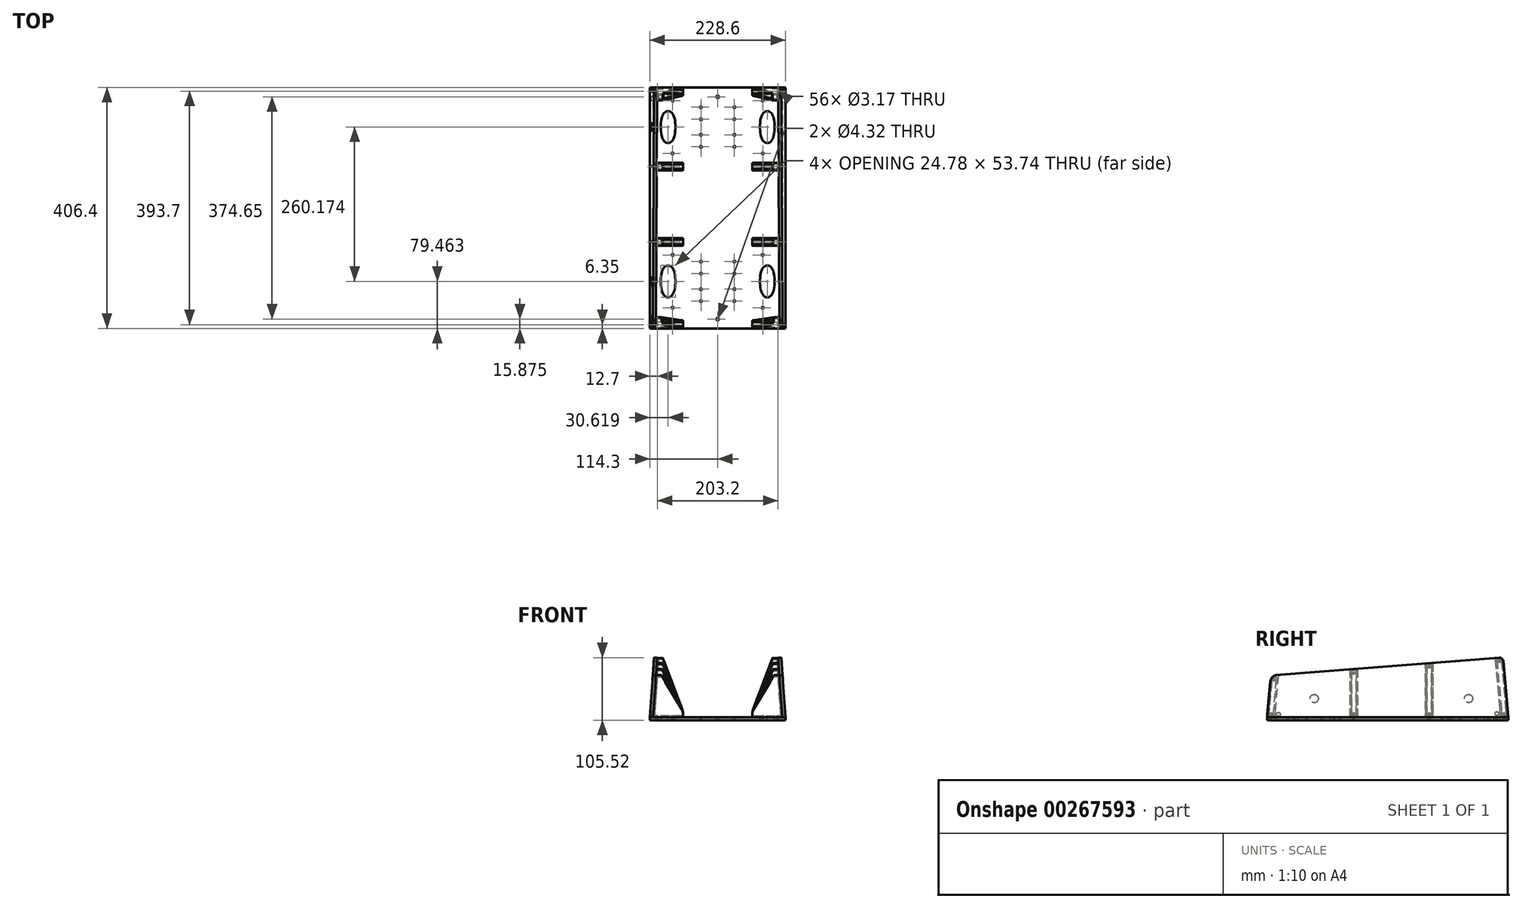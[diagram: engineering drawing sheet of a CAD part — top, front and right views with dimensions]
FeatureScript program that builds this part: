
annotation { "Feature Type Name" : "Feature", "Feature Type Description" : "" }
export const myFeature = defineFeature(function(context is Context, id is Id, definition is map)
    precondition{}
    {
        {
            var Q0;
            Q0=qCreatedBy(makeId("Top.planeOp"),FACE);
            var sketch = newSketch(context, id + "F0", { "sketchPlane" : qUnion([Q0])});
            skLineSegment(sketch, "E0.bottom", {"start": v(-114.3, 203.2) * mm, "end": v(114.3, 203.2) * mm});
            skLineSegment(sketch, "E0.top", {"start": v(-114.3, -203.2) * mm, "end": v(114.3, -203.2) * mm});
            skLineSegment(sketch, "E0.left", {"start": v(-114.3, 203.2) * mm, "end": v(-114.3, -203.2) * mm});
            skLineSegment(sketch, "E0.right", {"start": v(114.3, 203.2) * mm, "end": v(114.3, -203.2) * mm});
            skPoint(sketch, "E0.middle", {"position": v(0, 0) * mm});
            skSolve(sketch);
        }
        {
            var Q0;
            Q0=makeQuery(id+"F0.imprint","IMPRINT",FACE,{"disambiguationData":[TD([[makeQuery(id+"F0.imprint","IMPRINT",EDGE,{"derivedFrom":sQuery(id+"F0.wireOp",EDGE,"E0.bottom")}),-1.0]])]});
            extrude(context, id + "F1", {"entities" : qUnion([Q0]), "depth" : 5.08 * mm});
        }
        {
            var Q0;
            Q0=makeQuery(id+"F1.opExtrude","SWEPT_FACE",FACE,{"disambiguationData":[OSD([sQuery(id+"F0.wireOp",EDGE,"E0.bottom")])]});
            var sketch = newSketch(context, id + "F2", { "sketchPlane" : qUnion([Q0])});
            skLineSegment(sketch, "E1", {"start": v(114.3, 5.08) * mm, "end": v(107.2, 106.68) * mm});
            skLineSegment(sketch, "E2", {"start": v(107.2, 106.68) * mm, "end": v(102.13, 106.33) * mm});
            skLineSegment(sketch, "E3", {"start": v(102.13, 106.33) * mm, "end": v(109.2, 5.08) * mm});
            skLineSegment(sketch, "E4", {"start": v(109.2, 5.08) * mm, "end": v(114.3, 5.08) * mm});
            skSolve(sketch);
        }
        {
            var Q0;
            Q0=makeQuery(id+"F1.opExtrude","SWEPT_FACE",FACE,{"disambiguationData":[OSD([sQuery(id+"F0.wireOp",EDGE,"E0.top")])]});
            var sketch = newSketch(context, id + "F3", { "sketchPlane" : qUnion([Q0])});
            skLineSegment(sketch, "E5", {"start": v(-114.3, 5.08) * mm, "end": v(-109.42, 74.93) * mm});
            skLineSegment(sketch, "E6", {"start": v(-109.42, 74.93) * mm, "end": v(-104.35, 74.58) * mm});
            skLineSegment(sketch, "E7", {"start": v(-104.35, 74.58) * mm, "end": v(-109.2, 5.08) * mm});
            skLineSegment(sketch, "E8", {"start": v(-109.2, 5.08) * mm, "end": v(-114.3, 5.08) * mm});
            skSolve(sketch);
        }
        {
            var Q1;
            Q1=makeQuery(id+"F2.imprint","IMPRINT",FACE,{"disambiguationData":[TD([[makeQuery(id+"F2.imprint","IMPRINT",EDGE,{"derivedFrom":sQuery(id+"F2.wireOp",EDGE,"E1")}),1.0]])]});
            var Q2;
            Q2=makeQuery(id+"F3.imprint","IMPRINT",FACE,{"disambiguationData":[TD([[makeQuery(id+"F3.imprint","IMPRINT",EDGE,{"derivedFrom":sQuery(id+"F3.wireOp",EDGE,"E5")}),-1.0]])]});
            loft(context, id + "F4", {"sheetProfilesArray" : [{ "sheetProfileEntities" : qUnion([Q1]) }, { "sheetProfileEntities" : qUnion([Q2]) }]});
        }
        {
            var Q0;
            Q0=qCreatedBy(makeId("Right.planeOp"),FACE);
            var sketch = newSketch(context, id + "F5", { "sketchPlane" : qUnion([Q0])});
            skLineSegment(sketch, "E9", {"start": v(203.2, 5.08) * mm, "end": v(194.92, 99.72) * mm});
            skLineSegment(sketch, "E10", {"start": v(188.36, 122.29) * mm, "end": v(203.2, 122.29) * mm});
            skLineSegment(sketch, "E11", {"start": v(203.2, 122.29) * mm, "end": v(203.2, 5.08) * mm});
            skLineSegment(sketch, "E12", {"start": v(-203.2, 5.08) * mm, "end": v(-203.2, 91.13) * mm});
            skLineSegment(sketch, "E13", {"start": v(-203.2, 91.13) * mm, "end": v(-192.6, 91.13) * mm});
            skLineSegment(sketch, "E14", {"start": v(-197.97, 64.85) * mm, "end": v(-203.2, 5.08) * mm});
            skArc(sketch, "E15.filletArc", {"start": v(-188.23, 76.1) * mm, "mid": v(-194.92, 72.05) * mm, "end": v(-197.97, 64.85) * mm});
            skLineSegment(sketch, "E16", {"start": v(-192.6, 91.13) * mm, "end": v(-188.23, 76.1) * mm});
            skLineSegment(sketch, "E17", {"start": v(188.1, 105.5) * mm, "end": v(188.1, 105.5) * mm});
            skArc(sketch, "E18.filletArc", {"start": v(194.92, 99.72) * mm, "mid": v(192.7, 104.01) * mm, "end": v(188.1, 105.5) * mm});
            skLineSegment(sketch, "E19", {"start": v(188.1, 105.5) * mm, "end": v(188.36, 122.29) * mm});
            skSolve(sketch);
        }
        {
            var Q0;
            Q0=makeQuery(id+"F5.imprint","IMPRINT",FACE,{"disambiguationData":[TD([[makeQuery(id+"F5.imprint","IMPRINT",EDGE,{"derivedFrom":sQuery(id+"F5.wireOp",EDGE,"E9")}),-1.0]])]});
            var Q1;
            Q1=makeQuery(id+"F5.imprint","IMPRINT",FACE,{"disambiguationData":[TD([[makeQuery(id+"F5.imprint","IMPRINT",EDGE,{"derivedFrom":sQuery(id+"F5.wireOp",EDGE,"E12")}),-1.0]])]});
            extrude(context, id + "F6", {"entities" : qUnion([Q0, Q1]), "operationType" : NewBodyOperationType.REMOVE, "oppositeDirection" : true, "depth" : 203.2 * mm, "hasSecondDirection" : true, "secondDirectionOppositeDirection" : false, "secondDirectionDepth" : 147.32 * mm});
        }
        {
            var Q0;
            Q0=qCreatedBy(makeId("Front.planeOp"),FACE);
            cPlane(context, id + "F7", {"entities" : qUnion([Q0]), "cplaneType" : CPlaneType.OFFSET, "offset" : 127 * mm, "width" : 152.4 * mm, "height" : 152.4 * mm});
        }
        {
            var Q0;
            Q0=makeQuery(id+"F1.opExtrude","CAP_FACE",FACE,{"disambiguationData":[OSD([sQuery(id+"F0.wireOp",EDGE,"E0.bottom"),sQuery(id+"F0.wireOp",EDGE,"E0.top"),sQuery(id+"F0.wireOp",EDGE,"E0.left"),sQuery(id+"F0.wireOp",EDGE,"E0.right")])],"isStart":false});
            var sketch = newSketch(context, id + "F8", { "sketchPlane" : qUnion([Q0])});
            skCircle(sketch, "E20.0", {"center": v(-75.97, -168.27) * mm, "radius": 1.59 * mm});
            skCircle(sketch, "E21.0", {"center": v(-28.17, -157.07) * mm, "radius": 1.59 * mm});
            skCircle(sketch, "E22.0", {"center": v(-28.17, -136.9) * mm, "radius": 1.59 * mm});
            skCircle(sketch, "E23.0", {"center": v(-28.17, -110.58) * mm, "radius": 1.59 * mm});
            skCircle(sketch, "E24.0", {"center": v(-28.17, -90.4) * mm, "radius": 1.59 * mm});
            skCircle(sketch, "E25.0", {"center": v(-75.97, -79.2) * mm, "radius": 1.59 * mm});
            skFitSpline(sketch, "E26.0", {"points": [v(-83.68, -96.87) * mm, v(-83.23, -96.87) * mm, v(-82.57, -96.93) * mm, v(-81.73, -97.12) * mm, v(-80.9, -97.37) * mm, v(-79.92, -97.8) * mm, v(-78.87, -98.46) * mm, v(-77.94, -99.21) * mm, v(-77.13, -100.03) * mm, v(-76.43, -100.88) * mm, v(-75.8, -101.77) * mm, v(-75.26, -102.67) * mm, v(-74.78, -103.59) * mm, v(-74.35, -104.5) * mm, v(-73.85, -105.73) * mm, v(-73.32, -107.27) * mm, v(-72.81, -109.13) * mm, v(-72.4, -110.98) * mm, v(-71.98, -113.43) * mm, v(-71.6, -116.47) * mm, v(-71.37, -120.1) * mm, v(-71.29, -123.74) * mm, v(-71.37, -127.4) * mm, v(-71.61, -131.06) * mm, v(-71.99, -134.1) * mm, v(-72.42, -136.56) * mm, v(-72.83, -138.41) * mm, v(-73.34, -140.26) * mm, v(-73.87, -141.8) * mm, v(-74.38, -143.03) * mm, v(-74.8, -143.95) * mm, v(-75.29, -144.85) * mm, v(-75.83, -145.74) * mm, v(-76.44, -146.61) * mm, v(-77.15, -147.47) * mm, v(-77.96, -148.28) * mm, v(-78.88, -149.02) * mm, v(-79.75, -149.56) * mm, v(-80.5, -149.93) * mm, v(-81.1, -150.16) * mm, v(-81.72, -150.35) * mm, v(-82.57, -150.54) * mm, v(-83.24, -150.6) * mm, v(-83.68, -150.6) * mm]});
            skFitSpline(sketch, "E26.1", {"points": [v(-83.68, -96.87) * mm, v(-84.13, -96.87) * mm, v(-84.79, -96.93) * mm, v(-85.64, -97.12) * mm, v(-86.47, -97.37) * mm, v(-87.45, -97.8) * mm, v(-88.5, -98.46) * mm, v(-89.42, -99.21) * mm, v(-90.23, -100.03) * mm, v(-90.94, -100.88) * mm, v(-91.56, -101.77) * mm, v(-92.1, -102.67) * mm, v(-92.59, -103.59) * mm, v(-93, -104.5) * mm, v(-93.51, -105.73) * mm, v(-94.04, -107.27) * mm, v(-94.55, -109.13) * mm, v(-94.96, -110.98) * mm, v(-95.38, -113.43) * mm, v(-95.75, -116.47) * mm, v(-96, -120.1) * mm, v(-96.07, -123.74) * mm, v(-96, -127.4) * mm, v(-95.75, -131.06) * mm, v(-95.38, -134.1) * mm, v(-94.94, -136.56) * mm, v(-94.53, -138.41) * mm, v(-94.02, -140.26) * mm, v(-93.5, -141.8) * mm, v(-92.99, -143.03) * mm, v(-92.56, -143.95) * mm, v(-92.08, -144.85) * mm, v(-91.53, -145.74) * mm, v(-90.92, -146.61) * mm, v(-90.21, -147.47) * mm, v(-89.4, -148.28) * mm, v(-88.48, -149.02) * mm, v(-87.61, -149.56) * mm, v(-86.85, -149.93) * mm, v(-86.26, -150.16) * mm, v(-85.65, -150.35) * mm, v(-84.79, -150.54) * mm, v(-84.13, -150.6) * mm, v(-83.68, -150.6) * mm]});
            skLineSegment(sketch, "E27", {"start": v(-67.72, -127) * mm, "end": v(-28.17, -127) * mm, "construction": true});
            skLineSegment(sketch, "E28", {"start": v(-88.7, 6.35) * mm, "end": v(82.7, 6.35) * mm, "construction": true});
            skLineSegment(sketch, "E29", {"start": v(0, 92.42) * mm, "end": v(0, -98.09) * mm, "construction": true});
            skCircle(sketch, "E30.MirrorC", {"center": v(28.17, -136.9) * mm, "radius": 1.59 * mm});
            skCircle(sketch, "E31.MirrorC", {"center": v(28.17, -110.58) * mm, "radius": 1.59 * mm});
            skCircle(sketch, "E32.MirrorC", {"center": v(28.17, -157.07) * mm, "radius": 1.59 * mm});
            skCircle(sketch, "E33.MirrorC", {"center": v(75.97, -79.2) * mm, "radius": 1.59 * mm});
            skLineSegment(sketch, "E34.MirrorCS", {"start": v(67.72, -127) * mm, "end": v(28.17, -127) * mm, "construction": true});
            skCircle(sketch, "E35.MirrorC", {"center": v(28.17, -90.4) * mm, "radius": 1.59 * mm});
            skCircle(sketch, "E36.MirrorC", {"center": v(75.97, -168.27) * mm, "radius": 1.59 * mm});
            skFitSpline(sketch, "E37.MirrorCS", {"points": [v(83.68, -96.87) * mm, v(84.13, -96.87) * mm, v(84.79, -96.93) * mm, v(85.64, -97.12) * mm, v(86.47, -97.37) * mm, v(87.45, -97.8) * mm, v(88.5, -98.46) * mm, v(89.42, -99.21) * mm, v(90.23, -100.03) * mm, v(90.94, -100.88) * mm, v(91.56, -101.77) * mm, v(92.1, -102.67) * mm, v(92.59, -103.59) * mm, v(93, -104.5) * mm, v(93.51, -105.73) * mm, v(94.04, -107.27) * mm, v(94.55, -109.13) * mm, v(94.96, -110.98) * mm, v(95.38, -113.43) * mm, v(95.75, -116.47) * mm, v(96, -120.1) * mm, v(96.07, -123.74) * mm, v(96, -127.4) * mm, v(95.75, -131.06) * mm, v(95.38, -134.1) * mm, v(94.94, -136.56) * mm, v(94.53, -138.41) * mm, v(94.02, -140.26) * mm, v(93.5, -141.8) * mm, v(92.99, -143.03) * mm, v(92.56, -143.95) * mm, v(92.08, -144.85) * mm, v(91.53, -145.74) * mm, v(90.92, -146.61) * mm, v(90.21, -147.47) * mm, v(89.4, -148.28) * mm, v(88.48, -149.02) * mm, v(87.61, -149.56) * mm, v(86.85, -149.93) * mm, v(86.26, -150.16) * mm, v(85.65, -150.35) * mm, v(84.79, -150.54) * mm, v(84.13, -150.6) * mm, v(83.68, -150.6) * mm]});
            skFitSpline(sketch, "E38.MirrorCS", {"points": [v(83.68, -96.87) * mm, v(83.23, -96.87) * mm, v(82.57, -96.93) * mm, v(81.73, -97.12) * mm, v(80.9, -97.37) * mm, v(79.92, -97.8) * mm, v(78.87, -98.46) * mm, v(77.94, -99.21) * mm, v(77.13, -100.03) * mm, v(76.43, -100.88) * mm, v(75.8, -101.77) * mm, v(75.26, -102.67) * mm, v(74.78, -103.59) * mm, v(74.35, -104.5) * mm, v(73.85, -105.73) * mm, v(73.32, -107.27) * mm, v(72.81, -109.13) * mm, v(72.4, -110.98) * mm, v(71.98, -113.43) * mm, v(71.6, -116.47) * mm, v(71.37, -120.1) * mm, v(71.29, -123.74) * mm, v(71.37, -127.4) * mm, v(71.61, -131.06) * mm, v(71.99, -134.1) * mm, v(72.42, -136.56) * mm, v(72.83, -138.41) * mm, v(73.34, -140.26) * mm, v(73.87, -141.8) * mm, v(74.38, -143.03) * mm, v(74.8, -143.95) * mm, v(75.29, -144.85) * mm, v(75.83, -145.74) * mm, v(76.44, -146.61) * mm, v(77.15, -147.47) * mm, v(77.96, -148.28) * mm, v(78.88, -149.02) * mm, v(79.75, -149.56) * mm, v(80.5, -149.93) * mm, v(81.1, -150.16) * mm, v(81.72, -150.35) * mm, v(82.57, -150.54) * mm, v(83.24, -150.6) * mm, v(83.68, -150.6) * mm]});
            skCircle(sketch, "E39.MirrorC", {"center": v(28.17, 169.77) * mm, "radius": 1.59 * mm});
            skCircle(sketch, "E40.MirrorC", {"center": v(75.97, 91.9) * mm, "radius": 1.59 * mm});
            skCircle(sketch, "E41.MirrorC", {"center": v(28.17, 149.6) * mm, "radius": 1.59 * mm});
            skCircle(sketch, "E42.MirrorC", {"center": v(28.17, 123.28) * mm, "radius": 1.59 * mm});
            skCircle(sketch, "E43.MirrorC", {"center": v(75.97, 180.97) * mm, "radius": 1.59 * mm});
            skCircle(sketch, "E44.MirrorC", {"center": v(28.17, 103.1) * mm, "radius": 1.59 * mm});
            skLineSegment(sketch, "E45.MirrorCS", {"start": v(67.72, 139.7) * mm, "end": v(28.17, 139.7) * mm, "construction": true});
            skFitSpline(sketch, "E46.MirrorCS", {"points": [v(83.68, 109.57) * mm, v(84.13, 109.57) * mm, v(84.79, 109.63) * mm, v(85.64, 109.82) * mm, v(86.47, 110.07) * mm, v(87.45, 110.5) * mm, v(88.5, 111.16) * mm, v(89.42, 111.91) * mm, v(90.23, 112.73) * mm, v(90.94, 113.58) * mm, v(91.56, 114.47) * mm, v(92.1, 115.37) * mm, v(92.59, 116.29) * mm, v(93, 117.2) * mm, v(93.51, 118.43) * mm, v(94.04, 119.97) * mm, v(94.55, 121.83) * mm, v(94.96, 123.68) * mm, v(95.38, 126.13) * mm, v(95.75, 129.17) * mm, v(96, 132.8) * mm, v(96.07, 136.44) * mm, v(96, 140.1) * mm, v(95.75, 143.76) * mm, v(95.38, 146.8) * mm, v(94.94, 149.26) * mm, v(94.53, 151.11) * mm, v(94.02, 152.96) * mm, v(93.5, 154.5) * mm, v(92.99, 155.73) * mm, v(92.56, 156.65) * mm, v(92.08, 157.55) * mm, v(91.53, 158.44) * mm, v(90.92, 159.31) * mm, v(90.21, 160.17) * mm, v(89.4, 160.98) * mm, v(88.48, 161.72) * mm, v(87.61, 162.26) * mm, v(86.85, 162.63) * mm, v(86.26, 162.86) * mm, v(85.65, 163.05) * mm, v(84.79, 163.24) * mm, v(84.13, 163.3) * mm, v(83.68, 163.3) * mm]});
            skFitSpline(sketch, "E47.MirrorCS", {"points": [v(83.68, 109.57) * mm, v(83.23, 109.57) * mm, v(82.57, 109.63) * mm, v(81.73, 109.82) * mm, v(80.9, 110.07) * mm, v(79.92, 110.5) * mm, v(78.87, 111.16) * mm, v(77.94, 111.91) * mm, v(77.13, 112.73) * mm, v(76.43, 113.58) * mm, v(75.8, 114.47) * mm, v(75.26, 115.37) * mm, v(74.78, 116.29) * mm, v(74.35, 117.2) * mm, v(73.85, 118.43) * mm, v(73.32, 119.97) * mm, v(72.81, 121.83) * mm, v(72.4, 123.68) * mm, v(71.98, 126.13) * mm, v(71.6, 129.17) * mm, v(71.37, 132.8) * mm, v(71.29, 136.44) * mm, v(71.37, 140.1) * mm, v(71.61, 143.76) * mm, v(71.99, 146.8) * mm, v(72.42, 149.26) * mm, v(72.83, 151.11) * mm, v(73.34, 152.96) * mm, v(73.87, 154.5) * mm, v(74.38, 155.73) * mm, v(74.8, 156.65) * mm, v(75.29, 157.55) * mm, v(75.83, 158.44) * mm, v(76.44, 159.31) * mm, v(77.15, 160.17) * mm, v(77.96, 160.98) * mm, v(78.88, 161.72) * mm, v(79.75, 162.26) * mm, v(80.5, 162.63) * mm, v(81.1, 162.86) * mm, v(81.72, 163.05) * mm, v(82.57, 163.24) * mm, v(83.24, 163.3) * mm, v(83.68, 163.3) * mm]});
            skCircle(sketch, "E48.MirrorC", {"center": v(-28.17, 123.28) * mm, "radius": 1.59 * mm});
            skCircle(sketch, "E49.MirrorC", {"center": v(-75.97, 91.9) * mm, "radius": 1.59 * mm});
            skCircle(sketch, "E50.MirrorC", {"center": v(-28.17, 103.1) * mm, "radius": 1.59 * mm});
            skFitSpline(sketch, "E51.MirrorCS", {"points": [v(-83.68, 109.57) * mm, v(-83.23, 109.57) * mm, v(-82.57, 109.63) * mm, v(-81.73, 109.82) * mm, v(-80.9, 110.07) * mm, v(-79.92, 110.5) * mm, v(-78.87, 111.16) * mm, v(-77.94, 111.91) * mm, v(-77.13, 112.73) * mm, v(-76.43, 113.58) * mm, v(-75.8, 114.47) * mm, v(-75.26, 115.37) * mm, v(-74.78, 116.29) * mm, v(-74.35, 117.2) * mm, v(-73.85, 118.43) * mm, v(-73.32, 119.97) * mm, v(-72.81, 121.83) * mm, v(-72.4, 123.68) * mm, v(-71.98, 126.13) * mm, v(-71.6, 129.17) * mm, v(-71.37, 132.8) * mm, v(-71.29, 136.44) * mm, v(-71.37, 140.1) * mm, v(-71.61, 143.76) * mm, v(-71.99, 146.8) * mm, v(-72.42, 149.26) * mm, v(-72.83, 151.11) * mm, v(-73.34, 152.96) * mm, v(-73.87, 154.5) * mm, v(-74.38, 155.73) * mm, v(-74.8, 156.65) * mm, v(-75.29, 157.55) * mm, v(-75.83, 158.44) * mm, v(-76.44, 159.31) * mm, v(-77.15, 160.17) * mm, v(-77.96, 160.98) * mm, v(-78.88, 161.72) * mm, v(-79.75, 162.26) * mm, v(-80.5, 162.63) * mm, v(-81.1, 162.86) * mm, v(-81.72, 163.05) * mm, v(-82.57, 163.24) * mm, v(-83.24, 163.3) * mm, v(-83.68, 163.3) * mm]});
            skLineSegment(sketch, "E52.MirrorCS", {"start": v(-67.72, 139.7) * mm, "end": v(-28.17, 139.7) * mm, "construction": true});
            skCircle(sketch, "E53.MirrorC", {"center": v(-75.97, 180.97) * mm, "radius": 1.59 * mm});
            skCircle(sketch, "E54.MirrorC", {"center": v(-28.17, 169.77) * mm, "radius": 1.59 * mm});
            skCircle(sketch, "E55.MirrorC", {"center": v(-28.17, 149.6) * mm, "radius": 1.59 * mm});
            skFitSpline(sketch, "E56.MirrorCS", {"points": [v(-83.68, 109.57) * mm, v(-84.13, 109.57) * mm, v(-84.79, 109.63) * mm, v(-85.64, 109.82) * mm, v(-86.47, 110.07) * mm, v(-87.45, 110.5) * mm, v(-88.5, 111.16) * mm, v(-89.42, 111.91) * mm, v(-90.23, 112.73) * mm, v(-90.94, 113.58) * mm, v(-91.56, 114.47) * mm, v(-92.1, 115.37) * mm, v(-92.59, 116.29) * mm, v(-93, 117.2) * mm, v(-93.51, 118.43) * mm, v(-94.04, 119.97) * mm, v(-94.55, 121.83) * mm, v(-94.96, 123.68) * mm, v(-95.38, 126.13) * mm, v(-95.75, 129.17) * mm, v(-96, 132.8) * mm, v(-96.07, 136.44) * mm, v(-96, 140.1) * mm, v(-95.75, 143.76) * mm, v(-95.38, 146.8) * mm, v(-94.94, 149.26) * mm, v(-94.53, 151.11) * mm, v(-94.02, 152.96) * mm, v(-93.5, 154.5) * mm, v(-92.99, 155.73) * mm, v(-92.56, 156.65) * mm, v(-92.08, 157.55) * mm, v(-91.53, 158.44) * mm, v(-90.92, 159.31) * mm, v(-90.21, 160.17) * mm, v(-89.4, 160.98) * mm, v(-88.48, 161.72) * mm, v(-87.61, 162.26) * mm, v(-86.85, 162.63) * mm, v(-86.26, 162.86) * mm, v(-85.65, 163.05) * mm, v(-84.79, 163.24) * mm, v(-84.13, 163.3) * mm, v(-83.68, 163.3) * mm]});
            skPoint(sketch, "E57.middle", {"position": v(0, 0) * mm});
            skCircle(sketch, "E58", {"center": v(-101.6, -196.85) * mm, "radius": 1.59 * mm});
            skCircle(sketch, "E59", {"center": v(-76.2, -196.85) * mm, "radius": 1.59 * mm});
            skCircle(sketch, "E60.MirrorC", {"center": v(-76.2, -57.15) * mm, "radius": 1.59 * mm});
            skCircle(sketch, "E61.MirrorC", {"center": v(-101.6, -57.15) * mm, "radius": 1.59 * mm});
            skCircle(sketch, "E62", {"center": v(-101.6, 196.85) * mm, "radius": 1.59 * mm});
            skCircle(sketch, "E63", {"center": v(-76.2, 196.85) * mm, "radius": 1.59 * mm});
            skCircle(sketch, "E64.MirrorC", {"center": v(101.6, 196.85) * mm, "radius": 1.59 * mm});
            skCircle(sketch, "E65.MirrorC", {"center": v(76.2, 196.85) * mm, "radius": 1.59 * mm});
            skCircle(sketch, "E66.MirrorC", {"center": v(101.6, -57.15) * mm, "radius": 1.59 * mm});
            skCircle(sketch, "E67.MirrorC", {"center": v(76.2, -57.15) * mm, "radius": 1.59 * mm});
            skCircle(sketch, "E68.MirrorC", {"center": v(101.6, -196.85) * mm, "radius": 1.59 * mm});
            skCircle(sketch, "E69.MirrorC", {"center": v(76.2, -196.85) * mm, "radius": 1.59 * mm});
            skCircle(sketch, "E70", {"center": v(-101.6, 69.85) * mm, "radius": 1.59 * mm});
            skCircle(sketch, "E71", {"center": v(-76.2, 69.85) * mm, "radius": 1.59 * mm});
            skCircle(sketch, "E72.MirrorC", {"center": v(76.2, 69.85) * mm, "radius": 1.59 * mm});
            skCircle(sketch, "E73.MirrorC", {"center": v(101.6, 69.85) * mm, "radius": 1.59 * mm});
            skPoint(sketch, "E57.right.start.orphan", {"position": v(114.3, 203.2) * mm});
            skPoint(sketch, "E57.left.start.orphan", {"position": v(-114.3, 203.2) * mm});
            skPoint(sketch, "E57.top.end.orphan", {"position": v(114.3, -203.2) * mm});
            skPoint(sketch, "E57.top.start.orphan", {"position": v(-114.3, -203.2) * mm});
            skCircle(sketch, "E74", {"center": v(0, 187.33) * mm, "radius": 2.16 * mm});
            skCircle(sketch, "E75", {"center": v(0, -187.32) * mm, "radius": 2.16 * mm});
            skSolve(sketch);
        }
        {
            var Q0;
            Q0=makeQuery(id+"F4.opLoft","SWEPT_FACE",FACE,{"disambiguationData":[OSD([sQuery(id+"F0.wireOp",EDGE,"E0.bottom"),sQuery(id+"F0.wireOp",EDGE,"E0.top"),sQuery(id+"F0.wireOp",EDGE,"E0.left"),sQuery(id+"F2.wireOp",EDGE,"E1"),sQuery(id+"F2.wireOp",EDGE,"E2"),sQuery(id+"F2.wireOp",EDGE,"E4"),sQuery(id+"F3.wireOp",EDGE,"E5"),sQuery(id+"F3.wireOp",EDGE,"E6"),sQuery(id+"F3.wireOp",EDGE,"E8")])]});
            var sketch = newSketch(context, id + "F9", { "sketchPlane" : qUnion([Q0])});
            skLineSegment(sketch, "E76", {"start": v(197.97, 57) * mm, "end": v(197.97, 57) * mm});
            skLineSegment(sketch, "E77", {"start": v(196.83, -2.9) * mm, "end": v(190.63, 68.1) * mm, "construction": true});
            skLineSegment(sketch, "E78", {"start": v(-196.83, -2.9) * mm, "end": v(-188.04, 97.76) * mm, "construction": true});
            skLineSegment(sketch, "E79", {"start": v(-69.85, -2.9) * mm, "end": v(-69.85, 88.5) * mm, "construction": true});
            skLineSegment(sketch, "E80", {"start": v(57.15, -2.9) * mm, "end": v(57.15, 78.55) * mm, "construction": true});
            skCircle(sketch, "E81", {"center": v(-196.27, 3.42) * mm, "radius": 1.59 * mm});
            skCircle(sketch, "E82", {"center": v(-188.6, 91.43) * mm, "radius": 1.59 * mm});
            skCircle(sketch, "E83", {"center": v(-69.85, 82.15) * mm, "radius": 1.59 * mm});
            skCircle(sketch, "E84", {"center": v(-69.85, 3.44) * mm, "radius": 1.59 * mm});
            skCircle(sketch, "E85", {"center": v(57.15, 72.2) * mm, "radius": 1.59 * mm});
            skCircle(sketch, "E86", {"center": v(57.15, 3.44) * mm, "radius": 1.59 * mm});
            skCircle(sketch, "E87", {"center": v(196.27, 3.42) * mm, "radius": 1.59 * mm});
            skCircle(sketch, "E88", {"center": v(191.3, 60.5) * mm, "radius": 1.59 * mm});
            skCircle(sketch, "E89", {"center": v(184.15, 2.17) * mm, "radius": 3.24 * mm});
            skCircle(sketch, "E90", {"center": v(-184.15, 3.44) * mm, "radius": 3.24 * mm});
            skCircle(sketch, "E91", {"center": v(123.74, 28.84) * mm, "radius": 6.99 * mm});
            skCircle(sketch, "E92", {"center": v(-136.44, 28.84) * mm, "radius": 6.99 * mm});
            skSolve(sketch);
        }
        {
            var Q0;
            Q0=makeQuery(id+"F4.opLoft","SWEPT_BODY",BODY,{"disambiguationData":[OSD([makeQuery(id+"F2.imprint","IMPRINT",FACE,{"disambiguationData":[TD([[makeQuery(id+"F2.imprint","IMPRINT",EDGE,{"derivedFrom":sQuery(id+"F2.wireOp",EDGE,"E1")}),1.0]])]}),makeQuery(id+"F3.imprint","IMPRINT",FACE,{"disambiguationData":[TD([[makeQuery(id+"F3.imprint","IMPRINT",EDGE,{"derivedFrom":sQuery(id+"F3.wireOp",EDGE,"E5")}),-1.0]])]})])]});
            var Q1;
            Q1=qCreatedBy(makeId("Right.planeOp"),FACE);
            mirror(context, id + "F10", {"entities" : qUnion([Q0]), "mirrorPlane" : qUnion([Q1])});
        }
        {
            var Q0;
            Q0=makeQuery(id+"F6.boolean.opBoolean","COPY",FACE,{"derivedFrom":makeQuery(id+"F6.opExtrude","SWEPT_FACE",FACE,{"disambiguationData":[OSD([sQuery(id+"F5.wireOp",EDGE,"E14")])]})});
            cPlane(context, id + "F11", {"entities" : qUnion([Q0]), "cplaneType" : CPlaneType.OFFSET, "offset" : 0 * mm, "width" : 152.4 * mm, "height" : 152.4 * mm});
        }
        {
            var Q0;
            Q0=qCreatedBy(id+"F11.planeOp",FACE);
            var sketch = newSketch(context, id + "F12", { "sketchPlane" : qUnion([Q0])});
            skLineSegment(sketch, "E93", {"start": v(-58.4, -12.65) * mm, "end": v(-109.2, -12.65) * mm});
            skLineSegment(sketch, "E94", {"start": v(-109.2, -12.65) * mm, "end": v(-104.31, 57.6) * mm});
            skLineSegment(sketch, "E95", {"start": v(-104.31, 57.6) * mm, "end": v(-94.79, 57.6) * mm});
            skLineSegment(sketch, "E96", {"start": v(-94.79, 57.6) * mm, "end": v(-58.4, -3.12) * mm});
            skLineSegment(sketch, "E97", {"start": v(-58.4, -3.12) * mm, "end": v(-58.4, -12.65) * mm});
            skSolve(sketch);
        }
        {
            var Q0;
            Q0=qCreatedBy(id+"F11.planeOp",FACE);
            cPlane(context, id + "F13", {"entities" : qUnion([Q0]), "cplaneType" : CPlaneType.OFFSET, "offset" : 12.7 * mm, "oppositeDirection" : true, "width" : 152.4 * mm, "height" : 152.4 * mm});
        }
        {
            var Q0;
            Q0=qCreatedBy(id+"F13.planeOp",FACE);
            var sketch = newSketch(context, id + "F14", { "sketchPlane" : qUnion([Q0])});
            skLineSegment(sketch, "E98", {"start": v(-94.72, 59.7) * mm, "end": v(-58.4, -2.01) * mm});
            skLineSegment(sketch, "E99", {"start": v(-58.4, -2.01) * mm, "end": v(-58.4, -11.54) * mm});
            skLineSegment(sketch, "E100", {"start": v(-58.4, -11.54) * mm, "end": v(-109.2, -11.54) * mm});
            skLineSegment(sketch, "E101", {"start": v(-104.24, 59.7) * mm, "end": v(-94.72, 59.7) * mm});
            skLineSegment(sketch, "E102", {"start": v(-104.24, 59.7) * mm, "end": v(-109.2, -11.54) * mm});
            skSolve(sketch);
        }
        {
            var Q1;
            Q1=makeQuery(id+"F12.imprint","IMPRINT",FACE,{"disambiguationData":[TD([[makeQuery(id+"F12.imprint","IMPRINT",EDGE,{"derivedFrom":sQuery(id+"F12.wireOp",EDGE,"E93")}),-1.0]])]});
            var Q2;
            Q2=makeQuery(id+"F14.imprint","IMPRINT",FACE,{"disambiguationData":[TD([[makeQuery(id+"F14.imprint","IMPRINT",EDGE,{"derivedFrom":sQuery(id+"F14.wireOp",EDGE,"E98")}),-1.0]])]});
            loft(context, id + "F15", {"sheetProfilesArray" : [{ "sheetProfileEntities" : qUnion([Q1]) }, { "sheetProfileEntities" : qUnion([Q2]) }]});
        }
        {
            var Q0;
            Q0=makeQuery(id+"F15.opLoft","MID_CAP_EDGE",EDGE,{"disambiguationData":[OSD([sQuery(id+"F12.wireOp",EDGE,"E94"),sQuery(id+"F12.wireOp",EDGE,"E95"),sQuery(id+"F12.wireOp",EDGE,"E96")])],"capPos":0.0});
            fillet(context, id + "F16", {"entities" : qUnion([Q0]), "radius" : 12.7 * mm, "tangentPropagation" : true, "allowEdgeOverflow" : false});
        }
        {
            var Q0;
            Q0=makeQuery(id+"F15.opLoft","SWEPT_FACE",FACE,{"disambiguationData":[OSD([sQuery(id+"F12.wireOp",EDGE,"E95"),sQuery(id+"F12.wireOp",EDGE,"E96"),sQuery(id+"F12.wireOp",EDGE,"E97"),sQuery(id+"F14.wireOp",EDGE,"E98"),sQuery(id+"F14.wireOp",EDGE,"E99"),sQuery(id+"F14.wireOp",EDGE,"E101")])]});
            var Q1;
            Q1=makeQuery(id+"F15.opLoft","SWEPT_FACE",FACE,{"disambiguationData":[OSD([sQuery(id+"F12.wireOp",EDGE,"E93"),sQuery(id+"F12.wireOp",EDGE,"E96"),sQuery(id+"F12.wireOp",EDGE,"E97"),sQuery(id+"F14.wireOp",EDGE,"E98"),sQuery(id+"F14.wireOp",EDGE,"E99"),sQuery(id+"F14.wireOp",EDGE,"E100")])]});
            shell(context, id + "F17", {"entities" : qUnion([Q0, Q1]), "thickness" : 2.54 * mm});
        }
        {
            var Q0;
            Q0=sQuery(id+"F9.wireOp",EDGE,"E80");
            cPlane(context, id + "F18", {"entities" : qUnion([Q0]), "cplaneType" : CPlaneType.LINE_ANGLE, "offset" : 25.4 * mm, "angle" : 90 * degree, "width" : 152.4 * mm, "height" : 152.4 * mm});
        }
        {
            var Q0;
            Q0=qCreatedBy(id+"F18.planeOp",FACE);
            var sketch = newSketch(context, id + "F19", { "sketchPlane" : qUnion([Q0])});
            skLineSegment(sketch, "E103", {"start": v(103.5, 86.67) * mm, "end": v(93.98, 86.67) * mm});
            skLineSegment(sketch, "E104", {"start": v(93.98, 86.67) * mm, "end": v(58.4, 14.6) * mm});
            skLineSegment(sketch, "E105", {"start": v(58.4, 14.6) * mm, "end": v(58.4, 5.08) * mm});
            skLineSegment(sketch, "E106", {"start": v(58.4, 5.08) * mm, "end": v(109.2, 5.08) * mm});
            skLineSegment(sketch, "E107", {"start": v(109.2, 5.08) * mm, "end": v(103.5, 86.67) * mm});
            skSolve(sketch);
        }
        {
            var Q0;
            Q0=makeQuery(id+"F19.imprint","IMPRINT",FACE,{"disambiguationData":[TD([[makeQuery(id+"F19.imprint","IMPRINT",EDGE,{"derivedFrom":sQuery(id+"F19.wireOp",EDGE,"E103")}),1.0]])]});
            extrude(context, id + "F20", {"entities" : qUnion([Q0]), "depth" : 6.35 * mm, "hasSecondDirection" : true, "secondDirectionOppositeDirection" : true, "secondDirectionDepth" : 6.35 * mm});
        }
        {
            var Q0;
            Q0=qCreatedBy(makeId("Right.planeOp"),FACE);
            var sketch = newSketch(context, id + "F21", { "sketchPlane" : qUnion([Q0])});
            skLineSegment(sketch, "E108", {"start": v(-63.83, 85.46) * mm, "end": v(-49.7, 86.57) * mm});
            skLineSegment(sketch, "E109", {"start": v(-49.7, 86.57) * mm, "end": v(-49.7, 86.98) * mm});
            skLineSegment(sketch, "E110", {"start": v(-49.7, 86.98) * mm, "end": v(-63.84, 87.2) * mm});
            skLineSegment(sketch, "E111", {"start": v(-63.84, 87.2) * mm, "end": v(-63.83, 85.46) * mm});
            skSolve(sketch);
        }
        {
            var Q0;
            Q0=makeQuery(id+"F21.imprint","IMPRINT",FACE,{"disambiguationData":[TD([[makeQuery(id+"F21.imprint","IMPRINT",EDGE,{"derivedFrom":sQuery(id+"F21.wireOp",EDGE,"E108")}),1.0]])]});
            var Q1;
            Q1=makeQuery(id+"F20.opExtrude","SWEPT_FACE",FACE,{"disambiguationData":[OSD([sQuery(id+"F19.wireOp",EDGE,"E107")])]});
            extrude(context, id + "F22", {"entities" : qUnion([Q0]), "operationType" : NewBodyOperationType.REMOVE, "endBound" : BoundingType.UP_TO_SURFACE, "oppositeDirection" : true, "endBoundEntityFace" : qUnion([Q1]), "depth" : 25.4 * mm});
        }
        {
            var Q0;
            Q0=makeQuery(id+"F20.opExtrude","SWEPT_FACE",FACE,{"disambiguationData":[OSD([sQuery(id+"F19.wireOp",EDGE,"E104")])]});
            var Q1;
            Q1=makeQuery(id+"F20.opExtrude","SWEPT_FACE",FACE,{"disambiguationData":[OSD([sQuery(id+"F19.wireOp",EDGE,"E105")])]});
            shell(context, id + "F23", {"entities" : qUnion([Q0, Q1]), "thickness" : 2.54 * mm});
        }
        {
            var Q0;
            Q0=sQuery(id+"F9.wireOp",EDGE,"E79");
            cPlane(context, id + "F24", {"entities" : qUnion([Q0]), "cplaneType" : CPlaneType.LINE_ANGLE, "offset" : 25.4 * mm, "angle" : 90 * degree, "width" : 152.4 * mm, "height" : 152.4 * mm});
        }
        {
            var Q0;
            Q0=qCreatedBy(id+"F24.planeOp",FACE);
            var sketch = newSketch(context, id + "F25", { "sketchPlane" : qUnion([Q0])});
            skLineSegment(sketch, "E112", {"start": v(102.8, 96.7) * mm, "end": v(109.2, 5.08) * mm});
            skLineSegment(sketch, "E113", {"start": v(109.2, 5.08) * mm, "end": v(58.4, 5.08) * mm});
            skLineSegment(sketch, "E114", {"start": v(58.4, 5.08) * mm, "end": v(58.4, 14.6) * mm});
            skLineSegment(sketch, "E115", {"start": v(58.4, 14.6) * mm, "end": v(93.28, 96.7) * mm});
            skLineSegment(sketch, "E116", {"start": v(93.28, 96.7) * mm, "end": v(102.8, 96.7) * mm});
            skSolve(sketch);
        }
        {
            var Q0;
            Q0=makeQuery(id+"F25.imprint","IMPRINT",FACE,{"disambiguationData":[TD([[makeQuery(id+"F25.imprint","IMPRINT",EDGE,{"derivedFrom":sQuery(id+"F25.wireOp",EDGE,"E112")}),-1.0]])]});
            extrude(context, id + "F26", {"entities" : qUnion([Q0]), "depth" : 6.35 * mm, "hasSecondDirection" : true, "secondDirectionOppositeDirection" : true, "secondDirectionDepth" : 6.35 * mm});
        }
        {
            var Q0;
            Q0=qCreatedBy(makeId("Right.planeOp"),FACE);
            var sketch = newSketch(context, id + "F27", { "sketchPlane" : qUnion([Q0])});
            skLineSegment(sketch, "E117", {"start": v(79.55, 96.67) * mm, "end": v(60.68, 95.2) * mm});
            skLineSegment(sketch, "E118", {"start": v(60.68, 95.2) * mm, "end": v(60.68, 98.07) * mm});
            skLineSegment(sketch, "E119", {"start": v(60.68, 98.07) * mm, "end": v(79.55, 98.07) * mm});
            skLineSegment(sketch, "E120", {"start": v(79.55, 98.07) * mm, "end": v(79.55, 96.67) * mm});
            skSolve(sketch);
        }
        {
            var Q0;
            Q0=makeQuery(id+"F27.imprint","IMPRINT",FACE,{"disambiguationData":[TD([[makeQuery(id+"F27.imprint","IMPRINT",EDGE,{"derivedFrom":sQuery(id+"F27.wireOp",EDGE,"E117")}),-1.0]])]});
            var Q1;
            Q1=makeQuery(id+"F26.opExtrude","SWEPT_FACE",FACE,{"disambiguationData":[OSD([sQuery(id+"F25.wireOp",EDGE,"E112")])]});
            extrude(context, id + "F28", {"entities" : qUnion([Q0]), "operationType" : NewBodyOperationType.REMOVE, "endBound" : BoundingType.UP_TO_SURFACE, "oppositeDirection" : true, "endBoundEntityFace" : qUnion([Q1]), "depth" : 25.4 * mm});
        }
        {
            var Q0;
            Q0=makeQuery(id+"F26.opExtrude","SWEPT_FACE",FACE,{"disambiguationData":[OSD([sQuery(id+"F25.wireOp",EDGE,"E115")])]});
            var Q1;
            Q1=makeQuery(id+"F26.opExtrude","SWEPT_FACE",FACE,{"disambiguationData":[OSD([sQuery(id+"F25.wireOp",EDGE,"E114")])]});
            shell(context, id + "F29", {"entities" : qUnion([Q0, Q1]), "thickness" : 2.54 * mm});
        }
        {
            var Q0;
            Q0=makeQuery(id+"F6.boolean.opBoolean","COPY",FACE,{"derivedFrom":makeQuery(id+"F6.opExtrude","SWEPT_FACE",FACE,{"disambiguationData":[OSD([sQuery(id+"F5.wireOp",EDGE,"E9")])]})});
            cPlane(context, id + "F30", {"entities" : qUnion([Q0]), "cplaneType" : CPlaneType.OFFSET, "offset" : 0 * mm, "width" : 152.4 * mm, "height" : 152.4 * mm});
        }
        {
            var Q0;
            Q0=qCreatedBy(id+"F30.planeOp",FACE);
            cPlane(context, id + "F31", {"entities" : qUnion([Q0]), "cplaneType" : CPlaneType.OFFSET, "offset" : 12.7 * mm, "oppositeDirection" : true, "width" : 152.4 * mm, "height" : 152.4 * mm});
        }
        {
            var Q0;
            Q0=qCreatedBy(id+"F30.planeOp",FACE);
            var sketch = newSketch(context, id + "F32", { "sketchPlane" : qUnion([Q0])});
            skLineSegment(sketch, "E121", {"start": v(109.2, -12.65) * mm, "end": v(58.4, -12.65) * mm});
            skLineSegment(sketch, "E122", {"start": v(58.4, -12.65) * mm, "end": v(58.4, -3.12) * mm});
            skLineSegment(sketch, "E123", {"start": v(58.4, -3.12) * mm, "end": v(92.67, 87.96) * mm});
            skLineSegment(sketch, "E124", {"start": v(92.67, 87.96) * mm, "end": v(102.2, 87.96) * mm});
            skLineSegment(sketch, "E125", {"start": v(102.2, 87.96) * mm, "end": v(109.2, -12.65) * mm});
            skSolve(sketch);
        }
        {
            var Q0;
            Q0=qCreatedBy(id+"F31.planeOp",FACE);
            var sketch = newSketch(context, id + "F33", { "sketchPlane" : qUnion([Q0])});
            skLineSegment(sketch, "E126", {"start": v(102.25, 88.41) * mm, "end": v(109.2, -11.54) * mm});
            skLineSegment(sketch, "E127", {"start": v(109.2, -11.54) * mm, "end": v(58.4, -11.54) * mm});
            skLineSegment(sketch, "E128", {"start": v(58.4, -11.54) * mm, "end": v(58.4, -2.01) * mm});
            skLineSegment(sketch, "E129", {"start": v(58.4, -2.01) * mm, "end": v(92.72, 88.41) * mm});
            skLineSegment(sketch, "E130", {"start": v(92.72, 88.41) * mm, "end": v(102.25, 88.41) * mm});
            skSolve(sketch);
        }
        {
            var Q0;
            Q0=makeQuery(id+"F32.imprint","IMPRINT",FACE,{"disambiguationData":[TD([[makeQuery(id+"F32.imprint","IMPRINT",EDGE,{"derivedFrom":sQuery(id+"F32.wireOp",EDGE,"E121")}),-1.0]])]});
            var Q1;
            Q1=makeQuery(id+"F33.imprint","IMPRINT",FACE,{"disambiguationData":[TD([[makeQuery(id+"F33.imprint","IMPRINT",EDGE,{"derivedFrom":sQuery(id+"F33.wireOp",EDGE,"E126")}),-1.0]])]});
            loft(context, id + "F34", {"sheetProfilesArray" : [{ "sheetProfileEntities" : qUnion([Q0]) }, { "sheetProfileEntities" : qUnion([Q1]) }]});
        }
        {
            var Q0;
            Q0=makeQuery(id+"F34.opLoft","MID_CAP_EDGE",EDGE,{"disambiguationData":[OSD([sQuery(id+"F32.wireOp",EDGE,"E123"),sQuery(id+"F32.wireOp",EDGE,"E124"),sQuery(id+"F32.wireOp",EDGE,"E125")])],"capPos":0.0});
            fillet(context, id + "F35", {"entities" : qUnion([Q0]), "radius" : 6.35 * mm, "tangentPropagation" : true, "allowEdgeOverflow" : false});
        }
        {
            var Q0;
            Q0=makeQuery(id+"F34.opLoft","SWEPT_FACE",FACE,{"disambiguationData":[OSD([sQuery(id+"F32.wireOp",EDGE,"E122"),sQuery(id+"F32.wireOp",EDGE,"E123"),sQuery(id+"F32.wireOp",EDGE,"E124"),sQuery(id+"F33.wireOp",EDGE,"E128"),sQuery(id+"F33.wireOp",EDGE,"E129"),sQuery(id+"F33.wireOp",EDGE,"E130")])]});
            var Q1;
            Q1=makeQuery(id+"F34.opLoft","SWEPT_FACE",FACE,{"disambiguationData":[OSD([sQuery(id+"F32.wireOp",EDGE,"E121"),sQuery(id+"F32.wireOp",EDGE,"E122"),sQuery(id+"F32.wireOp",EDGE,"E123"),sQuery(id+"F33.wireOp",EDGE,"E127"),sQuery(id+"F33.wireOp",EDGE,"E128"),sQuery(id+"F33.wireOp",EDGE,"E129")])]});
            shell(context, id + "F36", {"entities" : qUnion([Q0, Q1]), "thickness" : 2.54 * mm});
        }
        {
            var Q0;
            Q0=makeQuery(id+"F15.opLoft","SWEPT_EDGE",EDGE,{"disambiguationData":[OSD([sQuery(id+"F12.wireOp",EDGE,"E96"),sQuery(id+"F12.wireOp",EDGE,"E97"),sQuery(id+"F14.wireOp",EDGE,"E98"),sQuery(id+"F14.wireOp",EDGE,"E99")])]});
            var Q1;
            Q1=makeQuery(id+"F17.opShell","OFFSET_EDGE",EDGE,{"disambiguationData":[OSD([sQuery(id+"F12.wireOp",EDGE,"E96"),sQuery(id+"F12.wireOp",EDGE,"E97"),sQuery(id+"F14.wireOp",EDGE,"E98"),sQuery(id+"F14.wireOp",EDGE,"E99")])]});
            var Q2;
            Q2=makeQuery(id+"F23.opShell","OFFSET_EDGE",EDGE,{"disambiguationData":[OSD([sQuery(id+"F19.wireOp",EDGE,"E104"),sQuery(id+"F19.wireOp",EDGE,"E105")])]});
            var Q3;
            Q3=makeQuery(id+"F20.opExtrude","SWEPT_EDGE",EDGE,{"disambiguationData":[OSD([sQuery(id+"F19.wireOp",EDGE,"E104"),sQuery(id+"F19.wireOp",EDGE,"E105")])]});
            var Q4;
            Q4=makeQuery(id+"F29.opShell","OFFSET_EDGE",EDGE,{"disambiguationData":[OSD([sQuery(id+"F25.wireOp",EDGE,"E114"),sQuery(id+"F25.wireOp",EDGE,"E115")])]});
            var Q5;
            Q5=makeQuery(id+"F26.opExtrude","SWEPT_EDGE",EDGE,{"disambiguationData":[OSD([sQuery(id+"F25.wireOp",EDGE,"E114"),sQuery(id+"F25.wireOp",EDGE,"E115")])]});
            var Q6;
            Q6=makeQuery(id+"F36.opShell","OFFSET_EDGE",EDGE,{"disambiguationData":[OSD([sQuery(id+"F32.wireOp",EDGE,"E122"),sQuery(id+"F32.wireOp",EDGE,"E123"),sQuery(id+"F33.wireOp",EDGE,"E128"),sQuery(id+"F33.wireOp",EDGE,"E129")])]});
            var Q7;
            Q7=makeQuery(id+"F34.opLoft","SWEPT_EDGE",EDGE,{"disambiguationData":[OSD([sQuery(id+"F32.wireOp",EDGE,"E122"),sQuery(id+"F32.wireOp",EDGE,"E123"),sQuery(id+"F33.wireOp",EDGE,"E128"),sQuery(id+"F33.wireOp",EDGE,"E129")])]});
            fillet(context, id + "F37", {"entities" : qUnion([Q0, Q1, Q2, Q3, Q4, Q5, Q6, Q7]), "radius" : 19.05 * mm, "tangentPropagation" : true, "allowEdgeOverflow" : false});
        }
        {
            var Q0;
            Q0 = qSketchRegion(id + "F9", true);
            var Q1;
            Q1=makeQuery(id+"F17.opShell","OFFSET_FACE",FACE,{"disambiguationData":[OSD([sQuery(id+"F12.wireOp",EDGE,"E93"),sQuery(id+"F12.wireOp",EDGE,"E94"),sQuery(id+"F12.wireOp",EDGE,"E95"),sQuery(id+"F14.wireOp",EDGE,"E100"),sQuery(id+"F14.wireOp",EDGE,"E101"),sQuery(id+"F14.wireOp",EDGE,"E102")])]});
            extrude(context, id + "F38", {"entities" : qUnion([Q0]), "operationType" : NewBodyOperationType.REMOVE, "oppositeDirection" : true, "endBoundEntityFace" : qUnion([Q1]), "depth" : 10.16 * mm});
        }
        {
            var Q0;
            Q0=makeQuery(id+"F15.opLoft","SWEPT_BODY",BODY,{"disambiguationData":[OSD([makeQuery(id+"F12.imprint","IMPRINT",FACE,{"disambiguationData":[TD([[makeQuery(id+"F12.imprint","IMPRINT",EDGE,{"derivedFrom":sQuery(id+"F12.wireOp",EDGE,"E93")}),-1.0]])]}),makeQuery(id+"F14.imprint","IMPRINT",FACE,{"disambiguationData":[TD([[makeQuery(id+"F14.imprint","IMPRINT",EDGE,{"derivedFrom":sQuery(id+"F14.wireOp",EDGE,"E98")}),-1.0]])]})])]});
            var Q1;
            Q1=makeQuery(id+"F20.opExtrude","SWEPT_BODY",BODY,{"disambiguationData":[OSD([sQuery(id+"F19.wireOp",EDGE,"E103"),sQuery(id+"F19.wireOp",EDGE,"E104"),sQuery(id+"F19.wireOp",EDGE,"E105"),sQuery(id+"F19.wireOp",EDGE,"E106"),sQuery(id+"F19.wireOp",EDGE,"E107")])]});
            var Q2;
            Q2=makeQuery(id+"F26.opExtrude","SWEPT_BODY",BODY,{"disambiguationData":[OSD([sQuery(id+"F25.wireOp",EDGE,"E112"),sQuery(id+"F25.wireOp",EDGE,"E113"),sQuery(id+"F25.wireOp",EDGE,"E114"),sQuery(id+"F25.wireOp",EDGE,"E115"),sQuery(id+"F25.wireOp",EDGE,"E116")])]});
            var Q3;
            Q3=makeQuery(id+"F34.opLoft","SWEPT_BODY",BODY,{"disambiguationData":[OSD([makeQuery(id+"F32.imprint","IMPRINT",FACE,{"disambiguationData":[TD([[makeQuery(id+"F32.imprint","IMPRINT",EDGE,{"derivedFrom":sQuery(id+"F32.wireOp",EDGE,"E121")}),-1.0]])]}),makeQuery(id+"F33.imprint","IMPRINT",FACE,{"disambiguationData":[TD([[makeQuery(id+"F33.imprint","IMPRINT",EDGE,{"derivedFrom":sQuery(id+"F33.wireOp",EDGE,"E126")}),-1.0]])]})])]});
            var Q4;
            Q4=qCreatedBy(makeId("Right.planeOp"),FACE);
            mirror(context, id + "F39", {"entities" : qUnion([Q0, Q1, Q2, Q3]), "mirrorPlane" : qUnion([Q4])});
        }
        {
            var Q0;
            Q0 = qSketchRegion(id + "F8", true);
            extrude(context, id + "F40", {"entities" : qUnion([Q0]), "operationType" : NewBodyOperationType.REMOVE, "oppositeDirection" : true, "depth" : 25.4 * mm, "hasSecondDirection" : true, "secondDirectionOppositeDirection" : false, "secondDirectionDepth" : 12.7 * mm});
        }
    });
